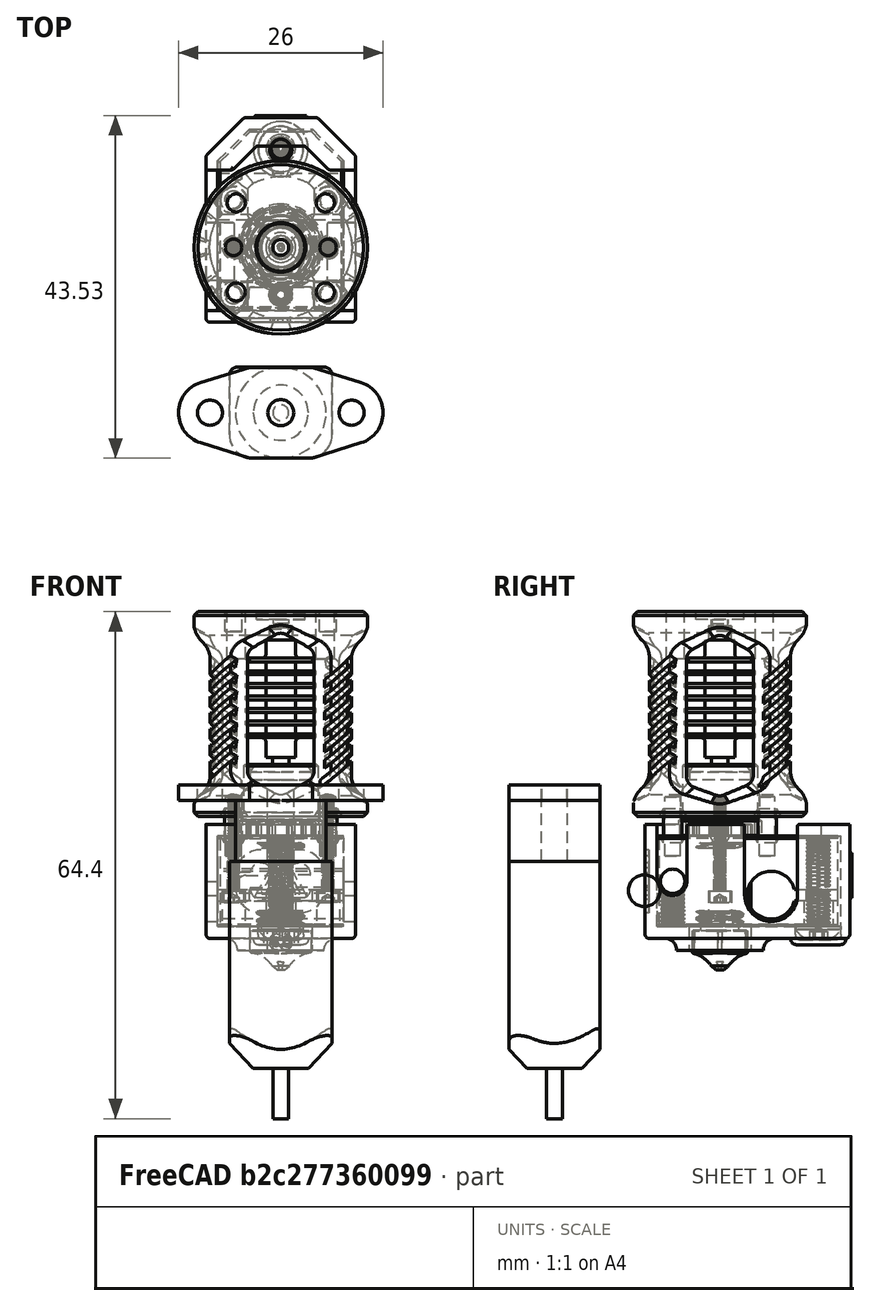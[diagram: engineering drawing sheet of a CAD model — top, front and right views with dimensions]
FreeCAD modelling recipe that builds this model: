
FCSTD DOCUMENT  (FreeCAD 1.0R39109 (Git))
Label: DELTOID_effector
License: All rights reserved
LicenseURL: https://en.wikipedia.org/wiki/All_rights_reserved
objects: Part::Feature×2, Assembly::JointGroup×1, PartDesign::Body×1, App::Part×1, Sketcher::SketchObject×1, Assembly::AssemblyObject×1
note: 5 computed .brp shape members not serialized (recipe doc carries the construction recipe); baked Part::Feature solids carry a one-line shape summary decoded from their .brp

FEATURE [Assembly::JointGroup] Joints
FEATURE [Part::Feature] Part__Feature  label="Voron Dragon HF\X2\5916
53D1\X0\"
  Placement = pos=(5e-16,0,-4) rot=(0.707107,-0.707107,0;3.14159rad)
  shape: bbox 22.2 x 27.9 x 47.19 mm, 951 faces (baked)
FEATURE [PartDesign::Body] Body  label="Corps"
  AllowCompound = false
  Origin = -> Origin002
FEATURE [App::Part] Part  label="EFFECTOR"
  Group = -> [Body]
  Origin = -> Origin001
FEATURE [Sketcher::SketchObject] Sketch
  ArcFitTolerance = 1e-06
  AttachmentSupport = -> [XY_Plane]
  FullyConstrained = true
  MakeInternals = false
  MapMode = 5
  sketch-geometry (7):
    g0: Circle CenterX=0 CenterY=0 CenterZ=0 NormalX=0 NormalY=0 NormalZ=1 AngleXU=0 Radius=25
    g1: LineSegment StartX=-20 StartY=25 StartZ=0 EndX=20 EndY=25 EndZ=0
    g2: LineSegment [constr] StartX=0 StartY=0 StartZ=0 EndX=0 EndY=25 EndZ=0
    g3: LineSegment [constr] StartX=0 StartY=0 StartZ=0 EndX=21.6506 EndY=-12.5 EndZ=0
    g4: LineSegment [constr] StartX=0 StartY=0 StartZ=0 EndX=-21.6506 EndY=-12.5 EndZ=0
    g5: LineSegment StartX=-31.6506 StartY=4.82051 StartZ=0 EndX=-11.6506 EndY=-29.8205 EndZ=0
    g6: LineSegment StartX=11.6506 StartY=-29.8205 StartZ=0 EndX=31.6506 EndY=4.82051 EndZ=0
  constraints (19):
    c: Coincident(g0,g-1)
    c: Symmetric(g1,g1,g-2)
    c: Tangent(g0,g1)
    c: Diameter(g0) = 50
    c: DistanceX(g1,g1) = 40
    c: Coincident(g2,g0)
    c: PointOnObject(g2,g0)
    c: Vertical(g2)
    c: Coincident(g3,g0)
    c: PointOnObject(g3,g0)
    c: Coincident(g4,g0)
    c: Tangent(g5,g0)
    c: Equal(g1,g6)
    c: Equal(g5,g6)
    c: Tangent(g6,g0)
    c: Symmetric(g6,g6,g3)
    c: Symmetric(g5,g5,g4)
    c: Symmetric(g4,g3,g-2)
    c: Angle(g4,g3) = 2.0944
FEATURE [Part::Feature] Part__Feature001  label="BL-touch"
  Placement = pos=(0,-21,0) rot=(0,0,1;3.14159rad)
  shape: bbox 26 x 15.81 x 42.4 mm, 39 faces (baked)
FEATURE [Assembly::AssemblyObject] Assembly
  Group = -> [Joints,Part__Feature001,Part__Feature]
  Origin = -> Origin
  Type = Assembly
